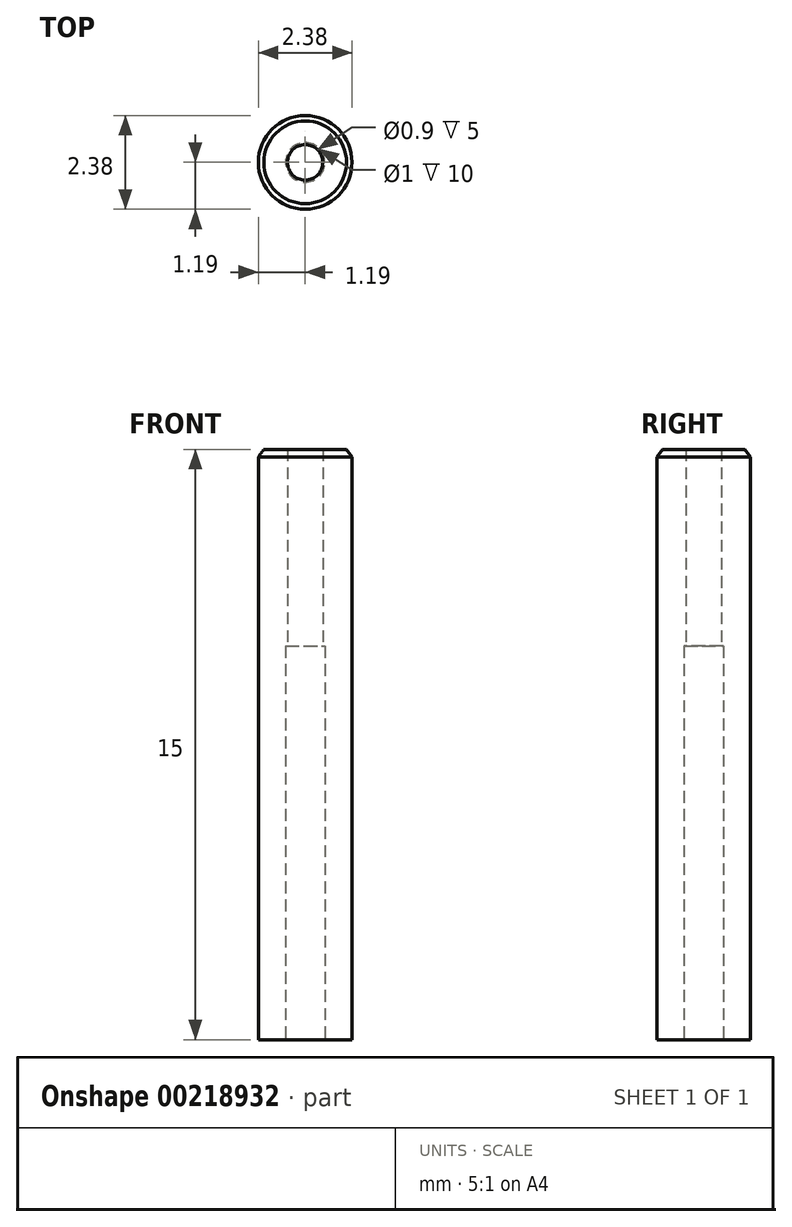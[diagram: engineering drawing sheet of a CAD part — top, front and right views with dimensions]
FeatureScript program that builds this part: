
annotation { "Feature Type Name" : "Feature", "Feature Type Description" : "" }
export const myFeature = defineFeature(function(context is Context, id is Id, definition is map)
    precondition{}
    {
        {
            var Q0;
            Q0=qCreatedBy(makeId("Right.planeOp"),FACE);
            var sketch = newSketch(context, id + "F0", { "sketchPlane" : qUnion([Q0])});
            skLineSegment(sketch, "E0", {"start": v(0, 0) * mm, "end": v(0, 15) * mm});
            skLineSegment(sketch, "E1", {"start": v(0, 15) * mm, "end": v(-1.05, 15) * mm});
            skLineSegment(sketch, "E2", {"start": v(-1.2, 14.8) * mm, "end": v(-1.19, 0) * mm});
            skLineSegment(sketch, "E3", {"start": v(-1.19, 0) * mm, "end": v(0, 0) * mm});
            skLineSegment(sketch, "E4", {"start": v(-1.05, 15) * mm, "end": v(-1.2, 14.8) * mm});
            skSolve(sketch);
        }
        {
            var Q0;
            Q0=makeQuery(id+"F0.imprint","IMPRINT",FACE,{"disambiguationData":[TD([[makeQuery(id+"F0.imprint","IMPRINT",EDGE,{"derivedFrom":sQuery(id+"F0.wireOp",EDGE,"E0")}),1.0]])]});
            var Q1;
            Q1=sQuery(id+"F0.wireOp",EDGE,"E0");
            revolve(context, id + "F1", {"entities" : qUnion([Q0]), "axis" : qUnion([Q1]), "revolveType" : RevolveType.FULL});
        }
        {
            var Q0;
            Q0=qCreatedBy(makeId("Top.planeOp"),FACE);
            var sketch = newSketch(context, id + "F2", { "sketchPlane" : qUnion([Q0])});
            skCircle(sketch, "E5", {"center": v(0, 0) * mm, "radius": 0.45 * mm});
            skSolve(sketch);
        }
        {
            var Q0;
            Q0=qSketchRegion(id+"F2",true);
            extrude(context, id + "F3", {"entities" : qUnion([Q0]), "operationType" : NewBodyOperationType.REMOVE, "depth" : 100 * mm});
        }
        {
            var Q0;
            Q0=makeQuery(id+"F1.opRevolve","SWEPT_FACE",FACE,{"disambiguationData":[OSD([sQuery(id+"F0.wireOp",EDGE,"E3")])]});
            var sketch = newSketch(context, id + "F4", { "sketchPlane" : qUnion([Q0])});
            skCircle(sketch, "E6", {"center": v(0, 0) * mm, "radius": 0.5 * mm});
            skSolve(sketch);
        }
        {
            var Q0;
            Q0=qSketchRegion(id+"F4",true);
            extrude(context, id + "F5", {"entities" : qUnion([Q0]), "operationType" : NewBodyOperationType.REMOVE, "oppositeDirection" : true, "depth" : 10 * mm});
        }
    });
